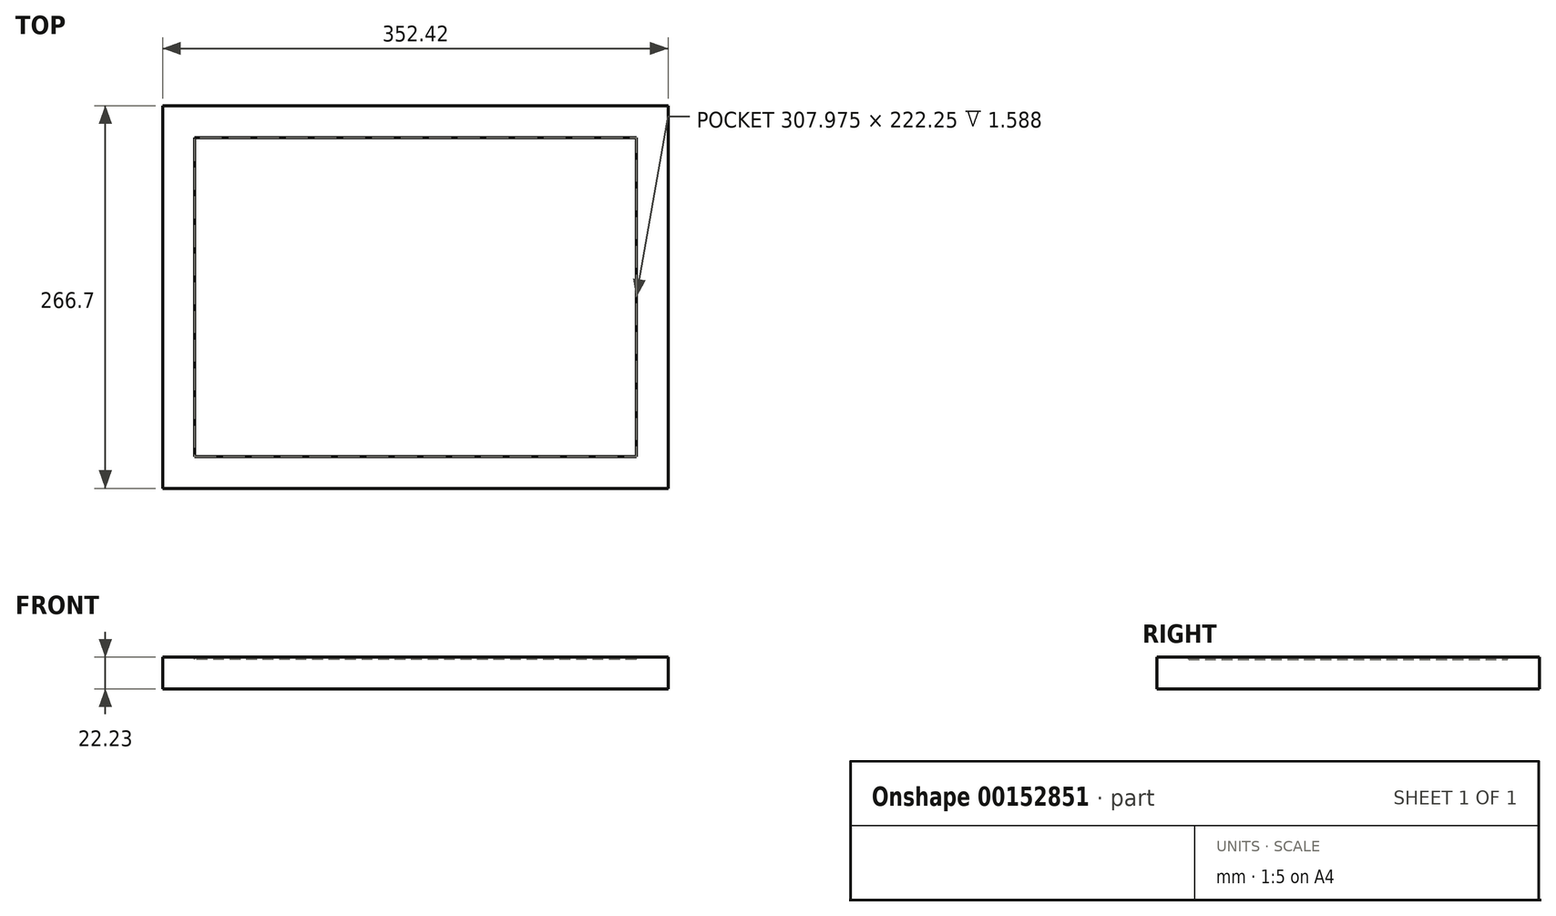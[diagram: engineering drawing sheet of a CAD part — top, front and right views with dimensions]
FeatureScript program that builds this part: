
annotation { "Feature Type Name" : "Feature", "Feature Type Description" : "" }
export const myFeature = defineFeature(function(context is Context, id is Id, definition is map)
    precondition{}
    {
        {
            var Q0;
            Q0=qCreatedBy(makeId("Top.planeOp"),FACE);
            var sketch = newSketch(context, id + "F0", { "sketchPlane" : qUnion([Q0])});
            skLineSegment(sketch, "E0.bottom", {"start": v(176.21, -133.35) * mm, "end": v(-176.21, -133.35) * mm});
            skLineSegment(sketch, "E0.top", {"start": v(176.21, 133.35) * mm, "end": v(-176.21, 133.35) * mm});
            skLineSegment(sketch, "E0.left", {"start": v(176.21, -133.35) * mm, "end": v(176.21, 133.35) * mm});
            skLineSegment(sketch, "E0.right", {"start": v(-176.21, -133.35) * mm, "end": v(-176.21, 133.35) * mm});
            skPoint(sketch, "E0.middle", {"position": v(0, 0) * mm});
            skSolve(sketch);
        }
        {
            var Q0;
            Q0=qSketchRegion(id+"F0",true);
            extrude(context, id + "F1", {"entities" : qUnion([Q0]), "depth" : 22.22 * mm});
        }
        {
            var Q0;
            Q0=makeQuery(id+"F1.opExtrude","CAP_FACE",FACE,{"disambiguationData":[OSD([sQuery(id+"F0.wireOp",EDGE,"E0.bottom"),sQuery(id+"F0.wireOp",EDGE,"E0.top"),sQuery(id+"F0.wireOp",EDGE,"E0.left"),sQuery(id+"F0.wireOp",EDGE,"E0.right")])],"isStart":false});
            var sketch = newSketch(context, id + "F2", { "sketchPlane" : qUnion([Q0])});
            skLineSegment(sketch, "E1.bottom", {"start": v(153.99, -111.13) * mm, "end": v(-153.99, -111.13) * mm});
            skLineSegment(sketch, "E1.top", {"start": v(153.99, 111.13) * mm, "end": v(-153.99, 111.13) * mm});
            skLineSegment(sketch, "E1.left", {"start": v(153.99, -111.13) * mm, "end": v(153.99, 111.13) * mm});
            skLineSegment(sketch, "E1.right", {"start": v(-153.99, -111.13) * mm, "end": v(-153.99, 111.13) * mm});
            skPoint(sketch, "E1.middle", {"position": v(0, 0) * mm});
            skSolve(sketch);
        }
        {
            var Q0;
            Q0 = qSketchRegion(id + "F2", true);
            extrude(context, id + "F3", {"entities" : qUnion([Q0]), "operationType" : NewBodyOperationType.REMOVE, "oppositeDirection" : true, "depth" : 1.59 * mm});
        }
    });
